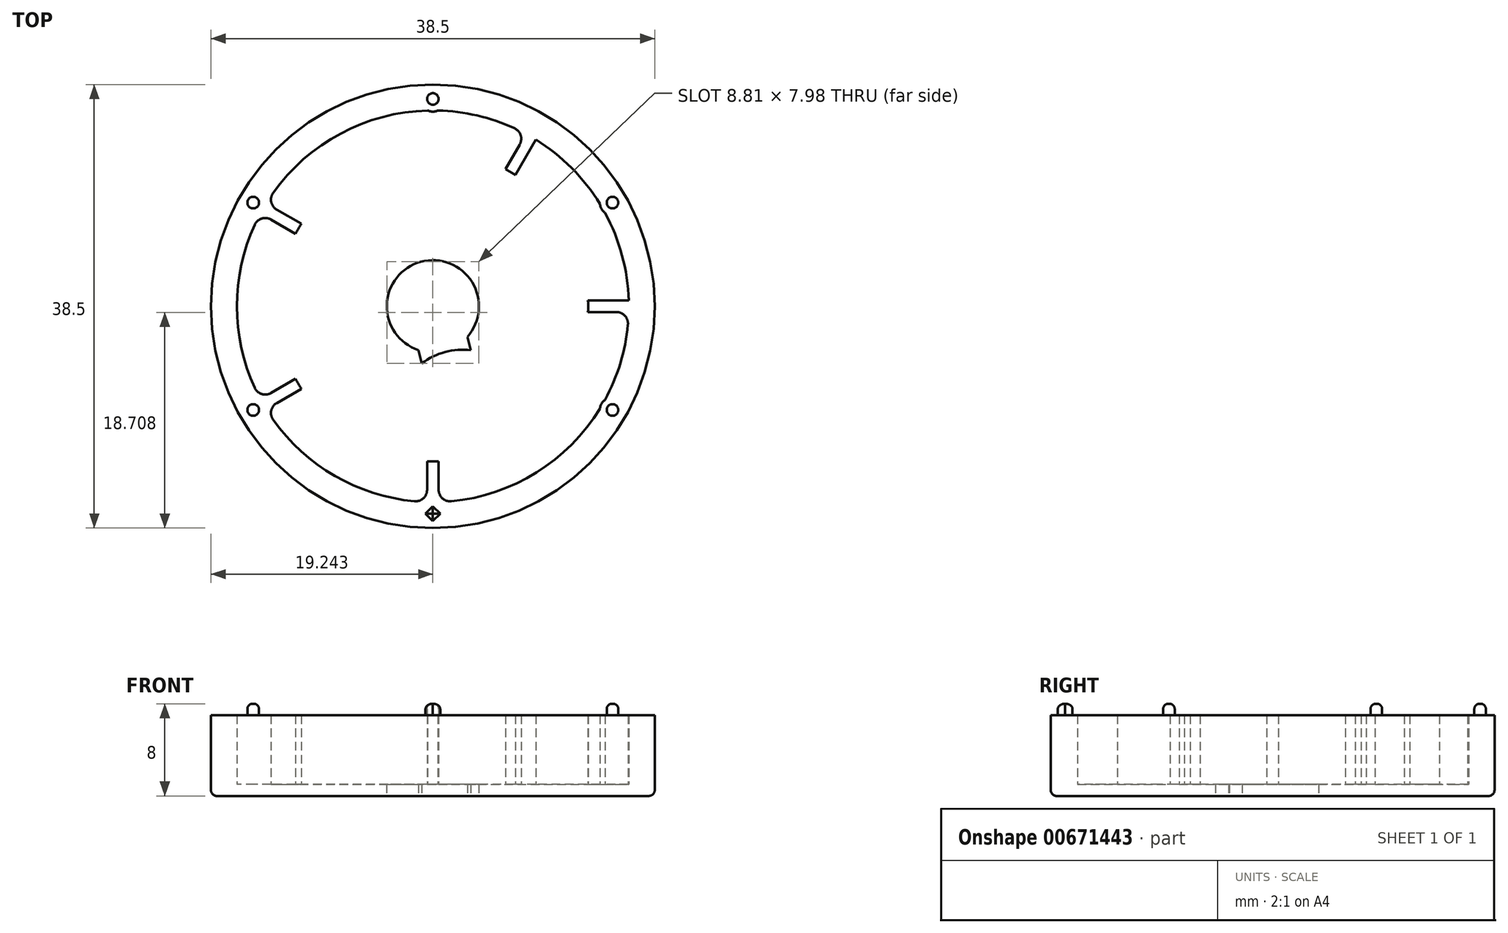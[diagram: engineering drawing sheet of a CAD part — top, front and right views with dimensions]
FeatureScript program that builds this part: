
annotation { "Feature Type Name" : "Feature", "Feature Type Description" : "" }
export const myFeature = defineFeature(function(context is Context, id is Id, definition is map)
    precondition{}
    {
        {
            var Q0;
            Q0=qCreatedBy(makeId("Top.planeOp"),FACE);
            var sketch = newSketch(context, id + "F0", { "sketchPlane" : qUnion([Q0])});
            skCircle(sketch, "E0", {"center": v(0, 0) * mm, "radius": 18 * mm});
            skCircle(sketch, "E1.0", {"center": v(0, 0) * mm, "radius": 17 * mm});
            skLineSegment(sketch, "E2.bottom", {"start": v(8.56, 15.83) * mm, "end": v(9.43, 15.33) * mm});
            skLineSegment(sketch, "E2.top", {"start": v(-9.43, -15.33) * mm, "end": v(-8.56, -15.83) * mm});
            skLineSegment(sketch, "E2.left", {"start": v(8.56, 15.83) * mm, "end": v(-9.43, -15.33) * mm});
            skLineSegment(sketch, "E2.right", {"start": v(9.43, 15.33) * mm, "end": v(-8.56, -15.83) * mm});
            skLineSegment(sketch, "E3.bottom", {"start": v(15.33, 9.43) * mm, "end": v(15.83, 8.56) * mm});
            skLineSegment(sketch, "E3.top", {"start": v(-15.83, -8.56) * mm, "end": v(-15.33, -9.43) * mm});
            skLineSegment(sketch, "E3.left", {"start": v(15.33, 9.43) * mm, "end": v(-15.83, -8.56) * mm});
            skLineSegment(sketch, "E3.right", {"start": v(15.83, 8.56) * mm, "end": v(-15.33, -9.43) * mm});
            skLineSegment(sketch, "E4", {"start": v(-38.35, 0) * mm, "end": v(39.17, 0) * mm, "construction": true});
            skLineSegment(sketch, "E5", {"start": v(0, 42.5) * mm, "end": v(0, -42.47) * mm, "construction": true});
            skLineSegment(sketch, "E6.bottom", {"start": v(-18, 0.5) * mm, "end": v(18, 0.5) * mm});
            skLineSegment(sketch, "E6.top", {"start": v(-18, -0.5) * mm, "end": v(18, -0.5) * mm});
            skLineSegment(sketch, "E6.left", {"start": v(-18, 0.5) * mm, "end": v(-18, -0.5) * mm});
            skLineSegment(sketch, "E6.right", {"start": v(18, 0.5) * mm, "end": v(18, -0.5) * mm});
            skLineSegment(sketch, "E7.bottom", {"start": v(-15.33, 9.43) * mm, "end": v(15.83, -8.56) * mm});
            skLineSegment(sketch, "E7.top", {"start": v(-15.83, 8.56) * mm, "end": v(15.33, -9.43) * mm});
            skLineSegment(sketch, "E7.left", {"start": v(-15.33, 9.43) * mm, "end": v(-15.83, 8.56) * mm});
            skLineSegment(sketch, "E7.right", {"start": v(15.83, -8.56) * mm, "end": v(15.33, -9.43) * mm});
            skLineSegment(sketch, "E8.bottom", {"start": v(-0.5, 18) * mm, "end": v(0.5, 18) * mm});
            skLineSegment(sketch, "E8.top", {"start": v(-0.5, -18) * mm, "end": v(0.5, -18) * mm});
            skLineSegment(sketch, "E8.left", {"start": v(-0.5, 18) * mm, "end": v(-0.5, -18) * mm});
            skLineSegment(sketch, "E8.right", {"start": v(0.5, 18) * mm, "end": v(0.5, -18) * mm});
            skLineSegment(sketch, "E9.bottom", {"start": v(-9.43, 15.33) * mm, "end": v(-8.56, 15.83) * mm});
            skLineSegment(sketch, "E9.top", {"start": v(8.56, -15.83) * mm, "end": v(9.43, -15.33) * mm});
            skLineSegment(sketch, "E9.left", {"start": v(-9.43, 15.33) * mm, "end": v(8.56, -15.83) * mm});
            skLineSegment(sketch, "E9.right", {"start": v(-8.56, 15.83) * mm, "end": v(9.43, -15.33) * mm});
            skCircle(sketch, "E10", {"center": v(0, 0) * mm, "radius": 13.47 * mm});
            skSolve(sketch);
        }
        {
            var Q0;
            Q0=qCreatedBy(makeId("Top.planeOp"),FACE);
            var sketch = newSketch(context, id + "F1", { "sketchPlane" : qUnion([Q0])});
            skCircle(sketch, "E11", {"center": v(0, 0) * mm, "radius": 19.25 * mm});
            skCircle(sketch, "E12", {"center": v(0, 0) * mm, "radius": 17 * mm});
            skSolve(sketch);
        }
        {
            var Q0;
            Q0=makeQuery(id+"F1.imprint","IMPRINT",FACE,{"disambiguationData":[TD([[makeQuery(id+"F1.imprint","IMPRINT",EDGE,{"derivedFrom":sQuery(id+"F1.wireOp",EDGE,"E11")}),1.0]])]});
            extrude(context, id + "F2", {"entities" : qUnion([Q0]), "depth" : 7 * mm, "offsetDistance" : 25 * mm});
        }
        {
            var Q0;
            Q0=qSketchRegion(id+"F1",true);
            var Q1;
            {var subQ0=sQuery(id+"F0.wireOp",EDGE,"E7.bottom");var subQ1=sQuery(id+"F0.wireOp",EDGE,"E1.0");var subQ2=makeQuery(id+"F0.imprint","INTERSECT",VERTEX,{"disambiguationData":[OD(0.0)],"derivedFrom":[subQ1,subQ0]});Q1=makeQuery(id+"F0.imprint","IMPRINT",FACE,{"disambiguationData":[TD([[makeQuery(id+"F0.imprint","IMPRINT",EDGE,{"disambiguationData":[TD([[subQ2,-1.0]])],"derivedFrom":subQ1}),1.0]])]});}
            var Q2;
            {var subQ0=sQuery(id+"F0.wireOp",EDGE,"E2.right");var subQ1=sQuery(id+"F0.wireOp",EDGE,"E1.0");var subQ2=makeQuery(id+"F0.imprint","INTERSECT",VERTEX,{"disambiguationData":[OD(0.0)],"derivedFrom":[subQ1,subQ0]});Q2=makeQuery(id+"F0.imprint","IMPRINT",FACE,{"disambiguationData":[TD([[makeQuery(id+"F0.imprint","IMPRINT",EDGE,{"disambiguationData":[TD([[subQ2,-1.0]])],"derivedFrom":subQ1}),1.0]])]});}
            var Q3;
            {var subQ0=sQuery(id+"F0.wireOp",EDGE,"E6.bottom");var subQ1=sQuery(id+"F0.wireOp",EDGE,"E1.0");var subQ2=makeQuery(id+"F0.imprint","INTERSECT",VERTEX,{"disambiguationData":[OD(0.0)],"derivedFrom":[subQ1,subQ0]});Q3=makeQuery(id+"F0.imprint","IMPRINT",FACE,{"disambiguationData":[TD([[makeQuery(id+"F0.imprint","IMPRINT",EDGE,{"disambiguationData":[TD([[subQ2,1.0]])],"derivedFrom":subQ1}),1.0]])]});}
            var Q4;
            {var subQ0=sQuery(id+"F0.wireOp",EDGE,"E8.left");var subQ1=sQuery(id+"F0.wireOp",EDGE,"E1.0");var subQ2=makeQuery(id+"F0.imprint","INTERSECT",VERTEX,{"disambiguationData":[OD(1.0)],"derivedFrom":[subQ1,subQ0]});Q4=makeQuery(id+"F0.imprint","IMPRINT",FACE,{"disambiguationData":[TD([[makeQuery(id+"F0.imprint","IMPRINT",EDGE,{"disambiguationData":[TD([[subQ2,-1.0]])],"derivedFrom":subQ1}),1.0]])]});}
            var Q5;
            {var subQ0=sQuery(id+"F0.wireOp",EDGE,"E3.left");var subQ1=sQuery(id+"F0.wireOp",EDGE,"E1.0");var subQ2=makeQuery(id+"F0.imprint","INTERSECT",VERTEX,{"disambiguationData":[OD(1.0)],"derivedFrom":[subQ1,subQ0]});Q5=makeQuery(id+"F0.imprint","IMPRINT",FACE,{"disambiguationData":[TD([[makeQuery(id+"F0.imprint","IMPRINT",EDGE,{"disambiguationData":[TD([[subQ2,-1.0]])],"derivedFrom":subQ1}),1.0]])]});}
            extrude(context, id + "F3", {"entities" : qUnion([Q0, Q1, Q2, Q3, Q4, Q5]), "operationType" : NewBodyOperationType.ADD, "depth" : 7 * mm, "offsetDistance" : 25 * mm});
        }
        {
            var Q0;
            Q0=makeQuery(id+"F1.imprint","IMPRINT",FACE,{"disambiguationData":[TD([[makeQuery(id+"F1.imprint","IMPRINT",EDGE,{"derivedFrom":sQuery(id+"F1.wireOp",EDGE,"E11")}),1.0]])]});
            var Q1;
            Q1=makeQuery(id+"F1.imprint","IMPRINT",FACE,{"disambiguationData":[TD([[makeQuery(id+"F1.imprint","IMPRINT",EDGE,{"derivedFrom":sQuery(id+"F1.wireOp",EDGE,"E12")}),1.0]])]});
            extrude(context, id + "F4", {"entities" : qUnion([Q0, Q1]), "operationType" : NewBodyOperationType.ADD, "depth" : 1 * mm, "offsetDistance" : 25 * mm});
        }
        {
            var Q0;
            Q0=qCreatedBy(makeId("Top.planeOp"),FACE);
            var sketch = newSketch(context, id + "F5", { "sketchPlane" : qUnion([Q0])});
            skCircle(sketch, "E13", {"center": v(0, 0) * mm, "radius": 18 * mm});
            skLineSegment(sketch, "E14", {"start": v(0, 18) * mm, "end": v(0, -18) * mm, "construction": true});
            skLineSegment(sketch, "E15", {"start": v(15.59, 9) * mm, "end": v(0, 0) * mm, "construction": true});
            skLineSegment(sketch, "E16", {"start": v(9, 15.59) * mm, "end": v(0, 0) * mm, "construction": true});
            skLineSegment(sketch, "E17", {"start": v(0, 0) * mm, "end": v(18, 0) * mm, "construction": true});
            skLineSegment(sketch, "E18", {"start": v(0, 0) * mm, "end": v(15.59, -9) * mm, "construction": true});
            skLineSegment(sketch, "E19", {"start": v(0, 0) * mm, "end": v(9, -15.59) * mm, "construction": true});
            skLineSegment(sketch, "E20", {"start": v(0, 0) * mm, "end": v(-9, 15.59) * mm, "construction": true});
            skLineSegment(sketch, "E21", {"start": v(0, 0) * mm, "end": v(-15.59, 9) * mm, "construction": true});
            skLineSegment(sketch, "E22", {"start": v(0, 0) * mm, "end": v(-18, 0) * mm, "construction": true});
            skLineSegment(sketch, "E23", {"start": v(0, 0) * mm, "end": v(-15.59, -9) * mm, "construction": true});
            skLineSegment(sketch, "E24", {"start": v(0, 0) * mm, "end": v(-9, -15.59) * mm, "construction": true});
            skCircle(sketch, "E25", {"center": v(0, 18) * mm, "radius": 1.1 * mm});
            skCircle(sketch, "E26", {"center": v(15.59, 9) * mm, "radius": 1.1 * mm});
            skCircle(sketch, "E27", {"center": v(15.59, -9) * mm, "radius": 1.1 * mm});
            skCircle(sketch, "E28", {"center": v(0, -18) * mm, "radius": 1.1 * mm});
            skCircle(sketch, "E29", {"center": v(-15.59, -9) * mm, "radius": 1.1 * mm});
            skCircle(sketch, "E30", {"center": v(-15.59, 9) * mm, "radius": 1.1 * mm});
            skCircle(sketch, "E31", {"center": v(-15.59, 9) * mm, "radius": 0.5 * mm});
            skCircle(sketch, "E32", {"center": v(0, 18) * mm, "radius": 0.5 * mm});
            skCircle(sketch, "E33", {"center": v(15.59, 9) * mm, "radius": 0.5 * mm});
            skCircle(sketch, "E34", {"center": v(15.59, -9) * mm, "radius": 0.5 * mm});
            skCircle(sketch, "E35", {"center": v(-15.59, -9) * mm, "radius": 0.5 * mm});
            skLineSegment(sketch, "E36.bottom", {"start": v(0.64, -18) * mm, "end": v(0, -18.64) * mm});
            skLineSegment(sketch, "E36.top", {"start": v(0, -17.36) * mm, "end": v(-0.64, -18) * mm});
            skLineSegment(sketch, "E36.left", {"start": v(0.64, -18) * mm, "end": v(0, -17.36) * mm});
            skLineSegment(sketch, "E36.right", {"start": v(0, -18.64) * mm, "end": v(-0.64, -18) * mm});
            skSolve(sketch);
        }
        {
            var Q0;
            {var subQ0=sQuery(id+"F5.wireOp",EDGE,"E30");var subQ1=sQuery(id+"F5.wireOp",EDGE,"E13");var subQ2=makeQuery(id+"F5.imprint","INTERSECT",VERTEX,{"disambiguationData":[OD(0.0)],"derivedFrom":[subQ1,subQ0]});Q0=makeQuery(id+"F5.imprint","IMPRINT",FACE,{"disambiguationData":[TD([[makeQuery(id+"F5.imprint","IMPRINT",EDGE,{"disambiguationData":[TD([[subQ2,-1.0]])],"derivedFrom":subQ1}),1.0]])]});}
            var Q1;
            {var subQ0=sQuery(id+"F5.wireOp",EDGE,"E30");var subQ1=sQuery(id+"F5.wireOp",EDGE,"E13");var subQ2=makeQuery(id+"F5.imprint","INTERSECT",VERTEX,{"disambiguationData":[OD(0.0)],"derivedFrom":[subQ1,subQ0]});Q1=makeQuery(id+"F5.imprint","IMPRINT",FACE,{"disambiguationData":[TD([[makeQuery(id+"F5.imprint","IMPRINT",EDGE,{"disambiguationData":[TD([[subQ2,-1.0]])],"derivedFrom":subQ1}),-1.0]])]});}
            var Q2;
            {var subQ0=sQuery(id+"F5.wireOp",EDGE,"E25");var subQ1=sQuery(id+"F5.wireOp",EDGE,"E13");var subQ2=makeQuery(id+"F5.imprint","INTERSECT",VERTEX,{"disambiguationData":[OD(0.0)],"derivedFrom":[subQ1,subQ0]});Q2=makeQuery(id+"F5.imprint","IMPRINT",FACE,{"disambiguationData":[TD([[makeQuery(id+"F5.imprint","IMPRINT",EDGE,{"disambiguationData":[TD([[subQ2,-1.0]])],"derivedFrom":subQ1}),1.0]])]});}
            var Q3;
            {var subQ0=sQuery(id+"F5.wireOp",EDGE,"E25");var subQ1=sQuery(id+"F5.wireOp",EDGE,"E13");var subQ2=makeQuery(id+"F5.imprint","INTERSECT",VERTEX,{"disambiguationData":[OD(0.0)],"derivedFrom":[subQ1,subQ0]});Q3=makeQuery(id+"F5.imprint","IMPRINT",FACE,{"disambiguationData":[TD([[makeQuery(id+"F5.imprint","IMPRINT",EDGE,{"disambiguationData":[TD([[subQ2,-1.0]])],"derivedFrom":subQ1}),-1.0]])]});}
            var Q4;
            {var subQ0=sQuery(id+"F5.wireOp",EDGE,"E26");var subQ1=sQuery(id+"F5.wireOp",EDGE,"E13");var subQ2=makeQuery(id+"F5.imprint","INTERSECT",VERTEX,{"disambiguationData":[OD(0.0)],"derivedFrom":[subQ1,subQ0]});Q4=makeQuery(id+"F5.imprint","IMPRINT",FACE,{"disambiguationData":[TD([[makeQuery(id+"F5.imprint","IMPRINT",EDGE,{"disambiguationData":[TD([[subQ2,-1.0]])],"derivedFrom":subQ1}),-1.0]])]});}
            var Q5;
            {var subQ0=sQuery(id+"F5.wireOp",EDGE,"E26");var subQ1=sQuery(id+"F5.wireOp",EDGE,"E13");var subQ2=makeQuery(id+"F5.imprint","INTERSECT",VERTEX,{"disambiguationData":[OD(0.0)],"derivedFrom":[subQ1,subQ0]});Q5=makeQuery(id+"F5.imprint","IMPRINT",FACE,{"disambiguationData":[TD([[makeQuery(id+"F5.imprint","IMPRINT",EDGE,{"disambiguationData":[TD([[subQ2,-1.0]])],"derivedFrom":subQ1}),1.0]])]});}
            var Q6;
            {var subQ0=sQuery(id+"F5.wireOp",EDGE,"E29");var subQ1=sQuery(id+"F5.wireOp",EDGE,"E13");var subQ2=makeQuery(id+"F5.imprint","INTERSECT",VERTEX,{"disambiguationData":[OD(0.0)],"derivedFrom":[subQ1,subQ0]});Q6=makeQuery(id+"F5.imprint","IMPRINT",FACE,{"disambiguationData":[TD([[makeQuery(id+"F5.imprint","IMPRINT",EDGE,{"disambiguationData":[TD([[subQ2,-1.0]])],"derivedFrom":subQ1}),1.0]])]});}
            var Q7;
            {var subQ0=sQuery(id+"F5.wireOp",EDGE,"E29");var subQ1=sQuery(id+"F5.wireOp",EDGE,"E13");var subQ2=makeQuery(id+"F5.imprint","INTERSECT",VERTEX,{"disambiguationData":[OD(0.0)],"derivedFrom":[subQ1,subQ0]});Q7=makeQuery(id+"F5.imprint","IMPRINT",FACE,{"disambiguationData":[TD([[makeQuery(id+"F5.imprint","IMPRINT",EDGE,{"disambiguationData":[TD([[subQ2,-1.0]])],"derivedFrom":subQ1}),-1.0]])]});}
            var Q8;
            {var subQ3=sQuery(id+"F5.wireOp",EDGE,"E13");var subQ5=sQuery(id+"F5.wireOp",EDGE,"E28");var subQ6=makeQuery(id+"F5.imprint","INTERSECT",VERTEX,{"disambiguationData":[OD(0.0)],"derivedFrom":[subQ3,subQ5]});Q8=makeQuery(id+"F5.imprint","IMPRINT",FACE,{"disambiguationData":[TD([[makeQuery(id+"F5.imprint","IMPRINT",EDGE,{"disambiguationData":[TD([[subQ6,-1.0]])],"derivedFrom":subQ3}),1.0]])]});}
            var Q9;
            {var subQ6=sQuery(id+"F5.wireOp",EDGE,"E36.bottom");Q9=makeQuery(id+"F5.imprint","IMPRINT",FACE,{"disambiguationData":[TD([[makeQuery(id+"F5.imprint","IMPRINT",EDGE,{"derivedFrom":subQ6}),1.0]])]});}
            var Q10;
            {var subQ0=sQuery(id+"F5.wireOp",EDGE,"E27");var subQ1=sQuery(id+"F5.wireOp",EDGE,"E13");var subQ2=makeQuery(id+"F5.imprint","INTERSECT",VERTEX,{"disambiguationData":[OD(0.0)],"derivedFrom":[subQ1,subQ0]});Q10=makeQuery(id+"F5.imprint","IMPRINT",FACE,{"disambiguationData":[TD([[makeQuery(id+"F5.imprint","IMPRINT",EDGE,{"disambiguationData":[TD([[subQ2,-1.0]])],"derivedFrom":subQ1}),-1.0]])]});}
            var Q11;
            {var subQ0=sQuery(id+"F5.wireOp",EDGE,"E27");var subQ1=sQuery(id+"F5.wireOp",EDGE,"E13");var subQ2=makeQuery(id+"F5.imprint","INTERSECT",VERTEX,{"disambiguationData":[OD(0.0)],"derivedFrom":[subQ1,subQ0]});Q11=makeQuery(id+"F5.imprint","IMPRINT",FACE,{"disambiguationData":[TD([[makeQuery(id+"F5.imprint","IMPRINT",EDGE,{"disambiguationData":[TD([[subQ2,-1.0]])],"derivedFrom":subQ1}),1.0]])]});}
            var Q12;
            {var subQ0=sQuery(id+"F5.wireOp",EDGE,"E31");var subQ1=sQuery(id+"F5.wireOp",EDGE,"E13");var subQ2=makeQuery(id+"F5.imprint","INTERSECT",VERTEX,{"disambiguationData":[OD(0.0)],"derivedFrom":[subQ1,subQ0]});Q12=makeQuery(id+"F5.imprint","IMPRINT",FACE,{"disambiguationData":[TD([[makeQuery(id+"F5.imprint","IMPRINT",EDGE,{"disambiguationData":[TD([[subQ2,-1.0]])],"derivedFrom":subQ1}),1.0]])]});}
            var Q13;
            {var subQ0=sQuery(id+"F5.wireOp",EDGE,"E31");var subQ1=sQuery(id+"F5.wireOp",EDGE,"E13");var subQ2=makeQuery(id+"F5.imprint","INTERSECT",VERTEX,{"disambiguationData":[OD(0.0)],"derivedFrom":[subQ1,subQ0]});Q13=makeQuery(id+"F5.imprint","IMPRINT",FACE,{"disambiguationData":[TD([[makeQuery(id+"F5.imprint","IMPRINT",EDGE,{"disambiguationData":[TD([[subQ2,-1.0]])],"derivedFrom":subQ1}),-1.0]])]});}
            var Q14;
            {var subQ0=sQuery(id+"F5.wireOp",EDGE,"E32");var subQ1=sQuery(id+"F5.wireOp",EDGE,"E13");var subQ2=makeQuery(id+"F5.imprint","INTERSECT",VERTEX,{"disambiguationData":[OD(0.0)],"derivedFrom":[subQ1,subQ0]});Q14=makeQuery(id+"F5.imprint","IMPRINT",FACE,{"disambiguationData":[TD([[makeQuery(id+"F5.imprint","IMPRINT",EDGE,{"disambiguationData":[TD([[subQ2,-1.0]])],"derivedFrom":subQ1}),-1.0]])]});}
            var Q15;
            {var subQ0=sQuery(id+"F5.wireOp",EDGE,"E32");var subQ1=sQuery(id+"F5.wireOp",EDGE,"E13");var subQ2=makeQuery(id+"F5.imprint","INTERSECT",VERTEX,{"disambiguationData":[OD(0.0)],"derivedFrom":[subQ1,subQ0]});Q15=makeQuery(id+"F5.imprint","IMPRINT",FACE,{"disambiguationData":[TD([[makeQuery(id+"F5.imprint","IMPRINT",EDGE,{"disambiguationData":[TD([[subQ2,-1.0]])],"derivedFrom":subQ1}),1.0]])]});}
            var Q16;
            {var subQ0=sQuery(id+"F5.wireOp",EDGE,"E33");var subQ1=sQuery(id+"F5.wireOp",EDGE,"E13");var subQ2=makeQuery(id+"F5.imprint","INTERSECT",VERTEX,{"disambiguationData":[OD(0.0)],"derivedFrom":[subQ1,subQ0]});Q16=makeQuery(id+"F5.imprint","IMPRINT",FACE,{"disambiguationData":[TD([[makeQuery(id+"F5.imprint","IMPRINT",EDGE,{"disambiguationData":[TD([[subQ2,-1.0]])],"derivedFrom":subQ1}),-1.0]])]});}
            var Q17;
            {var subQ0=sQuery(id+"F5.wireOp",EDGE,"E33");var subQ1=sQuery(id+"F5.wireOp",EDGE,"E13");var subQ2=makeQuery(id+"F5.imprint","INTERSECT",VERTEX,{"disambiguationData":[OD(0.0)],"derivedFrom":[subQ1,subQ0]});Q17=makeQuery(id+"F5.imprint","IMPRINT",FACE,{"disambiguationData":[TD([[makeQuery(id+"F5.imprint","IMPRINT",EDGE,{"disambiguationData":[TD([[subQ2,-1.0]])],"derivedFrom":subQ1}),1.0]])]});}
            var Q18;
            {var subQ0=sQuery(id+"F5.wireOp",EDGE,"E34");var subQ1=sQuery(id+"F5.wireOp",EDGE,"E13");var subQ2=makeQuery(id+"F5.imprint","INTERSECT",VERTEX,{"disambiguationData":[OD(0.0)],"derivedFrom":[subQ1,subQ0]});Q18=makeQuery(id+"F5.imprint","IMPRINT",FACE,{"disambiguationData":[TD([[makeQuery(id+"F5.imprint","IMPRINT",EDGE,{"disambiguationData":[TD([[subQ2,-1.0]])],"derivedFrom":subQ1}),-1.0]])]});}
            var Q19;
            {var subQ0=sQuery(id+"F5.wireOp",EDGE,"E34");var subQ1=sQuery(id+"F5.wireOp",EDGE,"E13");var subQ2=makeQuery(id+"F5.imprint","INTERSECT",VERTEX,{"disambiguationData":[OD(0.0)],"derivedFrom":[subQ1,subQ0]});Q19=makeQuery(id+"F5.imprint","IMPRINT",FACE,{"disambiguationData":[TD([[makeQuery(id+"F5.imprint","IMPRINT",EDGE,{"disambiguationData":[TD([[subQ2,-1.0]])],"derivedFrom":subQ1}),1.0]])]});}
            var Q20;
            {var subQ1=sQuery(id+"F5.wireOp",EDGE,"E36.bottom");Q20=makeQuery(id+"F5.imprint","IMPRINT",FACE,{"disambiguationData":[TD([[makeQuery(id+"F5.imprint","IMPRINT",EDGE,{"derivedFrom":subQ1}),-1.0]])]});}
            var Q21;
            {var subQ0=sQuery(id+"F5.wireOp",EDGE,"E35");var subQ1=sQuery(id+"F5.wireOp",EDGE,"E13");var subQ2=makeQuery(id+"F5.imprint","INTERSECT",VERTEX,{"disambiguationData":[OD(0.0)],"derivedFrom":[subQ1,subQ0]});Q21=makeQuery(id+"F5.imprint","IMPRINT",FACE,{"disambiguationData":[TD([[makeQuery(id+"F5.imprint","IMPRINT",EDGE,{"disambiguationData":[TD([[subQ2,-1.0]])],"derivedFrom":subQ1}),-1.0]])]});}
            var Q22;
            {var subQ0=sQuery(id+"F5.wireOp",EDGE,"E35");var subQ1=sQuery(id+"F5.wireOp",EDGE,"E13");var subQ2=makeQuery(id+"F5.imprint","INTERSECT",VERTEX,{"disambiguationData":[OD(0.0)],"derivedFrom":[subQ1,subQ0]});Q22=makeQuery(id+"F5.imprint","IMPRINT",FACE,{"disambiguationData":[TD([[makeQuery(id+"F5.imprint","IMPRINT",EDGE,{"disambiguationData":[TD([[subQ2,-1.0]])],"derivedFrom":subQ1}),1.0]])]});}
            var Q23;
            {var subQ0=sQuery(id+"F5.wireOp",EDGE,"E36.top");var subQ1=sQuery(id+"F5.wireOp",EDGE,"E13");var subQ2=makeQuery(id+"F5.imprint","INTERSECT",VERTEX,{"derivedFrom":[subQ1,subQ0]});Q23=makeQuery(id+"F5.imprint","IMPRINT",FACE,{"disambiguationData":[TD([[makeQuery(id+"F5.imprint","IMPRINT",EDGE,{"disambiguationData":[TD([[subQ2,-1.0]])],"derivedFrom":subQ1}),1.0]])]});}
            extrude(context, id + "F6", {"entities" : qUnion([Q0, Q1, Q2, Q3, Q4, Q5, Q6, Q7, Q8, Q9, Q10, Q11, Q12, Q13, Q14, Q15, Q16, Q17, Q18, Q19, Q20, Q21, Q22, Q23]), "operationType" : NewBodyOperationType.ADD, "depth" : 7 * mm, "offsetDistance" : 25 * mm});
        }
        {
            var Q0;
            {var subQ0=sQuery(id+"F0.wireOp",EDGE,"E8.right");var subQ1=sQuery(id+"F0.wireOp",EDGE,"E1.0");Q0=makeQuery(id+"F3.opExtrude","SWEPT_EDGE",EDGE,{"disambiguationData":[OSD([subQ1,subQ0]),TDD([makeQuery(id+"F0.imprint","INTERSECT",VERTEX,{"disambiguationData":[OD(1.0)],"derivedFrom":[subQ1,subQ0]})])]});}
            var Q1;
            {var subQ0=sQuery(id+"F0.wireOp",EDGE,"E2.left");var subQ1=sQuery(id+"F0.wireOp",EDGE,"E1.0");Q1=makeQuery(id+"F3.opExtrude","SWEPT_EDGE",EDGE,{"disambiguationData":[OSD([subQ1,subQ0]),TDD([makeQuery(id+"F0.imprint","INTERSECT",VERTEX,{"disambiguationData":[OD(1.0)],"derivedFrom":[subQ1,subQ0]})])]});}
            var Q2;
            {var subQ0=sQuery(id+"F0.wireOp",EDGE,"E3.left");var subQ1=sQuery(id+"F0.wireOp",EDGE,"E1.0");Q2=makeQuery(id+"F3.opExtrude","SWEPT_EDGE",EDGE,{"disambiguationData":[OSD([subQ1,subQ0]),TDD([makeQuery(id+"F0.imprint","INTERSECT",VERTEX,{"disambiguationData":[OD(1.0)],"derivedFrom":[subQ1,subQ0]})])]});}
            var Q3;
            {var subQ0=sQuery(id+"F0.wireOp",EDGE,"E6.bottom");var subQ1=sQuery(id+"F0.wireOp",EDGE,"E1.0");Q3=makeQuery(id+"F3.opExtrude","SWEPT_EDGE",EDGE,{"disambiguationData":[OSD([subQ1,subQ0]),TDD([makeQuery(id+"F0.imprint","INTERSECT",VERTEX,{"disambiguationData":[OD(1.0)],"derivedFrom":[subQ1,subQ0]})])]});}
            var Q4;
            {var subQ0=sQuery(id+"F0.wireOp",EDGE,"E9.right");var subQ1=sQuery(id+"F0.wireOp",EDGE,"E1.0");Q4=makeQuery(id+"F3.opExtrude","SWEPT_EDGE",EDGE,{"disambiguationData":[OSD([subQ1,subQ0]),TDD([makeQuery(id+"F0.imprint","INTERSECT",VERTEX,{"disambiguationData":[OD(1.0)],"derivedFrom":[subQ1,subQ0]})])]});}
            var Q5;
            {var subQ0=sQuery(id+"F0.wireOp",EDGE,"E7.bottom");var subQ1=sQuery(id+"F0.wireOp",EDGE,"E1.0");Q5=makeQuery(id+"F3.opExtrude","SWEPT_EDGE",EDGE,{"disambiguationData":[OSD([subQ1,subQ0]),TDD([makeQuery(id+"F0.imprint","INTERSECT",VERTEX,{"disambiguationData":[OD(1.0)],"derivedFrom":[subQ1,subQ0]})])]});}
            var Q6;
            {var subQ0=sQuery(id+"F0.wireOp",EDGE,"E8.left");var subQ1=sQuery(id+"F0.wireOp",EDGE,"E1.0");Q6=makeQuery(id+"F3.opExtrude","SWEPT_EDGE",EDGE,{"disambiguationData":[OSD([subQ1,subQ0]),TDD([makeQuery(id+"F0.imprint","INTERSECT",VERTEX,{"disambiguationData":[OD(0.0)],"derivedFrom":[subQ1,subQ0]})])]});}
            var Q7;
            {var subQ0=sQuery(id+"F0.wireOp",EDGE,"E2.left");var subQ1=sQuery(id+"F0.wireOp",EDGE,"E1.0");Q7=makeQuery(id+"F3.opExtrude","SWEPT_EDGE",EDGE,{"disambiguationData":[OSD([subQ1,subQ0]),TDD([makeQuery(id+"F0.imprint","INTERSECT",VERTEX,{"disambiguationData":[OD(0.0)],"derivedFrom":[subQ1,subQ0]})])]});}
            var Q8;
            {var subQ0=sQuery(id+"F0.wireOp",EDGE,"E3.left");var subQ1=sQuery(id+"F0.wireOp",EDGE,"E1.0");Q8=makeQuery(id+"F3.opExtrude","SWEPT_EDGE",EDGE,{"disambiguationData":[OSD([subQ1,subQ0]),TDD([makeQuery(id+"F0.imprint","INTERSECT",VERTEX,{"disambiguationData":[OD(0.0)],"derivedFrom":[subQ1,subQ0]})])]});}
            var Q9;
            {var subQ0=sQuery(id+"F0.wireOp",EDGE,"E6.top");var subQ1=sQuery(id+"F0.wireOp",EDGE,"E1.0");Q9=makeQuery(id+"F3.opExtrude","SWEPT_EDGE",EDGE,{"disambiguationData":[OSD([subQ1,subQ0]),TDD([makeQuery(id+"F0.imprint","INTERSECT",VERTEX,{"disambiguationData":[OD(1.0)],"derivedFrom":[subQ1,subQ0]})])]});}
            var Q10;
            {var subQ0=sQuery(id+"F0.wireOp",EDGE,"E7.top");var subQ1=sQuery(id+"F0.wireOp",EDGE,"E1.0");Q10=makeQuery(id+"F3.opExtrude","SWEPT_EDGE",EDGE,{"disambiguationData":[OSD([subQ1,subQ0]),TDD([makeQuery(id+"F0.imprint","INTERSECT",VERTEX,{"disambiguationData":[OD(0.0)],"derivedFrom":[subQ1,subQ0]})])]});}
            var Q11;
            {var subQ0=sQuery(id+"F0.wireOp",EDGE,"E6.top");var subQ1=sQuery(id+"F0.wireOp",EDGE,"E1.0");Q11=makeQuery(id+"F3.opExtrude","SWEPT_EDGE",EDGE,{"disambiguationData":[OSD([subQ1,subQ0]),TDD([makeQuery(id+"F0.imprint","INTERSECT",VERTEX,{"disambiguationData":[OD(0.0)],"derivedFrom":[subQ1,subQ0]})])]});}
            var Q12;
            {var subQ0=sQuery(id+"F0.wireOp",EDGE,"E9.left");var subQ1=sQuery(id+"F0.wireOp",EDGE,"E1.0");Q12=makeQuery(id+"F3.opExtrude","SWEPT_EDGE",EDGE,{"disambiguationData":[OSD([subQ1,subQ0]),TDD([makeQuery(id+"F0.imprint","INTERSECT",VERTEX,{"disambiguationData":[OD(0.0)],"derivedFrom":[subQ1,subQ0]})])]});}
            var Q13;
            {var subQ0=sQuery(id+"F0.wireOp",EDGE,"E8.right");var subQ1=sQuery(id+"F0.wireOp",EDGE,"E1.0");Q13=makeQuery(id+"F3.opExtrude","SWEPT_EDGE",EDGE,{"disambiguationData":[OSD([subQ1,subQ0]),TDD([makeQuery(id+"F0.imprint","INTERSECT",VERTEX,{"disambiguationData":[OD(0.0)],"derivedFrom":[subQ1,subQ0]})])]});}
            var Q14;
            {var subQ0=sQuery(id+"F0.wireOp",EDGE,"E7.bottom");var subQ1=sQuery(id+"F0.wireOp",EDGE,"E1.0");Q14=makeQuery(id+"F3.opExtrude","SWEPT_EDGE",EDGE,{"disambiguationData":[OSD([subQ1,subQ0]),TDD([makeQuery(id+"F0.imprint","INTERSECT",VERTEX,{"disambiguationData":[OD(0.0)],"derivedFrom":[subQ1,subQ0]})])]});}
            var Q15;
            {var subQ0=sQuery(id+"F0.wireOp",EDGE,"E9.right");var subQ1=sQuery(id+"F0.wireOp",EDGE,"E1.0");Q15=makeQuery(id+"F3.opExtrude","SWEPT_EDGE",EDGE,{"disambiguationData":[OSD([subQ1,subQ0]),TDD([makeQuery(id+"F0.imprint","INTERSECT",VERTEX,{"disambiguationData":[OD(0.0)],"derivedFrom":[subQ1,subQ0]})])]});}
            var Q16;
            {var subQ0=sQuery(id+"F0.wireOp",EDGE,"E3.right");var subQ1=sQuery(id+"F0.wireOp",EDGE,"E1.0");Q16=makeQuery(id+"F3.opExtrude","SWEPT_EDGE",EDGE,{"disambiguationData":[OSD([subQ1,subQ0]),TDD([makeQuery(id+"F0.imprint","INTERSECT",VERTEX,{"disambiguationData":[OD(1.0)],"derivedFrom":[subQ1,subQ0]})])]});}
            var Q17;
            {var subQ0=sQuery(id+"F0.wireOp",EDGE,"E2.right");var subQ1=sQuery(id+"F0.wireOp",EDGE,"E1.0");Q17=makeQuery(id+"F3.opExtrude","SWEPT_EDGE",EDGE,{"disambiguationData":[OSD([subQ1,subQ0]),TDD([makeQuery(id+"F0.imprint","INTERSECT",VERTEX,{"disambiguationData":[OD(1.0)],"derivedFrom":[subQ1,subQ0]})])]});}
            var Q18;
            {var subQ0=sQuery(id+"F0.wireOp",EDGE,"E3.right");var subQ1=sQuery(id+"F0.wireOp",EDGE,"E1.0");Q18=makeQuery(id+"F3.opExtrude","SWEPT_EDGE",EDGE,{"disambiguationData":[OSD([subQ1,subQ0]),TDD([makeQuery(id+"F0.imprint","INTERSECT",VERTEX,{"disambiguationData":[OD(0.0)],"derivedFrom":[subQ1,subQ0]})])]});}
            var Q19;
            {var subQ0=sQuery(id+"F0.wireOp",EDGE,"E2.right");var subQ1=sQuery(id+"F0.wireOp",EDGE,"E1.0");Q19=makeQuery(id+"F3.opExtrude","SWEPT_EDGE",EDGE,{"disambiguationData":[OSD([subQ1,subQ0]),TDD([makeQuery(id+"F0.imprint","INTERSECT",VERTEX,{"disambiguationData":[OD(0.0)],"derivedFrom":[subQ1,subQ0]})])]});}
            var Q20;
            {var subQ0=sQuery(id+"F0.wireOp",EDGE,"E8.left");var subQ1=sQuery(id+"F0.wireOp",EDGE,"E1.0");Q20=makeQuery(id+"F3.opExtrude","SWEPT_EDGE",EDGE,{"disambiguationData":[OSD([subQ1,subQ0]),TDD([makeQuery(id+"F0.imprint","INTERSECT",VERTEX,{"disambiguationData":[OD(1.0)],"derivedFrom":[subQ1,subQ0]})])]});}
            var Q21;
            {var subQ0=sQuery(id+"F0.wireOp",EDGE,"E9.left");var subQ1=sQuery(id+"F0.wireOp",EDGE,"E1.0");Q21=makeQuery(id+"F3.opExtrude","SWEPT_EDGE",EDGE,{"disambiguationData":[OSD([subQ1,subQ0]),TDD([makeQuery(id+"F0.imprint","INTERSECT",VERTEX,{"disambiguationData":[OD(1.0)],"derivedFrom":[subQ1,subQ0]})])]});}
            var Q22;
            {var subQ0=sQuery(id+"F0.wireOp",EDGE,"E7.top");var subQ1=sQuery(id+"F0.wireOp",EDGE,"E1.0");Q22=makeQuery(id+"F3.opExtrude","SWEPT_EDGE",EDGE,{"disambiguationData":[OSD([subQ1,subQ0]),TDD([makeQuery(id+"F0.imprint","INTERSECT",VERTEX,{"disambiguationData":[OD(1.0)],"derivedFrom":[subQ1,subQ0]})])]});}
            var Q23;
            {var subQ0=sQuery(id+"F0.wireOp",EDGE,"E6.bottom");var subQ1=sQuery(id+"F0.wireOp",EDGE,"E1.0");Q23=makeQuery(id+"F3.opExtrude","SWEPT_EDGE",EDGE,{"disambiguationData":[OSD([subQ1,subQ0]),TDD([makeQuery(id+"F0.imprint","INTERSECT",VERTEX,{"disambiguationData":[OD(0.0)],"derivedFrom":[subQ1,subQ0]})])]});}
            fillet(context, id + "F7", {"entities" : qUnion([Q0, Q1, Q2, Q3, Q4, Q5, Q6, Q7, Q8, Q9, Q10, Q11, Q12, Q13, Q14, Q15, Q16, Q17, Q18, Q19, Q20, Q21, Q22, Q23]), "radius" : 1 * mm, "tangentPropagation" : true, "allowEdgeOverflow" : false});
        }
        {
            var Q0;
            {var subQ0=sQuery(id+"F5.wireOp",EDGE,"E31");var subQ1=sQuery(id+"F5.wireOp",EDGE,"E13");var subQ2=makeQuery(id+"F5.imprint","INTERSECT",VERTEX,{"disambiguationData":[OD(0.0)],"derivedFrom":[subQ1,subQ0]});Q0=makeQuery(id+"F5.imprint","IMPRINT",FACE,{"disambiguationData":[TD([[makeQuery(id+"F5.imprint","IMPRINT",EDGE,{"disambiguationData":[TD([[subQ2,-1.0]])],"derivedFrom":subQ1}),-1.0]])]});}
            var Q1;
            {var subQ0=sQuery(id+"F5.wireOp",EDGE,"E31");var subQ1=sQuery(id+"F5.wireOp",EDGE,"E13");var subQ2=makeQuery(id+"F5.imprint","INTERSECT",VERTEX,{"disambiguationData":[OD(0.0)],"derivedFrom":[subQ1,subQ0]});Q1=makeQuery(id+"F5.imprint","IMPRINT",FACE,{"disambiguationData":[TD([[makeQuery(id+"F5.imprint","IMPRINT",EDGE,{"disambiguationData":[TD([[subQ2,-1.0]])],"derivedFrom":subQ1}),1.0]])]});}
            var Q2;
            {var subQ0=sQuery(id+"F5.wireOp",EDGE,"E32");var subQ1=sQuery(id+"F5.wireOp",EDGE,"E13");var subQ2=makeQuery(id+"F5.imprint","INTERSECT",VERTEX,{"disambiguationData":[OD(0.0)],"derivedFrom":[subQ1,subQ0]});Q2=makeQuery(id+"F5.imprint","IMPRINT",FACE,{"disambiguationData":[TD([[makeQuery(id+"F5.imprint","IMPRINT",EDGE,{"disambiguationData":[TD([[subQ2,-1.0]])],"derivedFrom":subQ1}),-1.0]])]});}
            var Q3;
            {var subQ0=sQuery(id+"F5.wireOp",EDGE,"E32");var subQ1=sQuery(id+"F5.wireOp",EDGE,"E13");var subQ2=makeQuery(id+"F5.imprint","INTERSECT",VERTEX,{"disambiguationData":[OD(0.0)],"derivedFrom":[subQ1,subQ0]});Q3=makeQuery(id+"F5.imprint","IMPRINT",FACE,{"disambiguationData":[TD([[makeQuery(id+"F5.imprint","IMPRINT",EDGE,{"disambiguationData":[TD([[subQ2,-1.0]])],"derivedFrom":subQ1}),1.0]])]});}
            var Q4;
            {var subQ0=sQuery(id+"F5.wireOp",EDGE,"E33");var subQ1=sQuery(id+"F5.wireOp",EDGE,"E13");var subQ2=makeQuery(id+"F5.imprint","INTERSECT",VERTEX,{"disambiguationData":[OD(0.0)],"derivedFrom":[subQ1,subQ0]});Q4=makeQuery(id+"F5.imprint","IMPRINT",FACE,{"disambiguationData":[TD([[makeQuery(id+"F5.imprint","IMPRINT",EDGE,{"disambiguationData":[TD([[subQ2,-1.0]])],"derivedFrom":subQ1}),1.0]])]});}
            var Q5;
            {var subQ0=sQuery(id+"F5.wireOp",EDGE,"E33");var subQ1=sQuery(id+"F5.wireOp",EDGE,"E13");var subQ2=makeQuery(id+"F5.imprint","INTERSECT",VERTEX,{"disambiguationData":[OD(0.0)],"derivedFrom":[subQ1,subQ0]});Q5=makeQuery(id+"F5.imprint","IMPRINT",FACE,{"disambiguationData":[TD([[makeQuery(id+"F5.imprint","IMPRINT",EDGE,{"disambiguationData":[TD([[subQ2,-1.0]])],"derivedFrom":subQ1}),-1.0]])]});}
            var Q6;
            {var subQ0=sQuery(id+"F5.wireOp",EDGE,"E34");var subQ1=sQuery(id+"F5.wireOp",EDGE,"E13");var subQ2=makeQuery(id+"F5.imprint","INTERSECT",VERTEX,{"disambiguationData":[OD(0.0)],"derivedFrom":[subQ1,subQ0]});Q6=makeQuery(id+"F5.imprint","IMPRINT",FACE,{"disambiguationData":[TD([[makeQuery(id+"F5.imprint","IMPRINT",EDGE,{"disambiguationData":[TD([[subQ2,-1.0]])],"derivedFrom":subQ1}),1.0]])]});}
            var Q7;
            {var subQ0=sQuery(id+"F5.wireOp",EDGE,"E34");var subQ1=sQuery(id+"F5.wireOp",EDGE,"E13");var subQ2=makeQuery(id+"F5.imprint","INTERSECT",VERTEX,{"disambiguationData":[OD(0.0)],"derivedFrom":[subQ1,subQ0]});Q7=makeQuery(id+"F5.imprint","IMPRINT",FACE,{"disambiguationData":[TD([[makeQuery(id+"F5.imprint","IMPRINT",EDGE,{"disambiguationData":[TD([[subQ2,-1.0]])],"derivedFrom":subQ1}),-1.0]])]});}
            var Q8;
            {var subQ1=sQuery(id+"F5.wireOp",EDGE,"E36.bottom");Q8=makeQuery(id+"F5.imprint","IMPRINT",FACE,{"disambiguationData":[TD([[makeQuery(id+"F5.imprint","IMPRINT",EDGE,{"derivedFrom":subQ1}),-1.0]])]});}
            var Q9;
            {var subQ0=sQuery(id+"F5.wireOp",EDGE,"E36.top");var subQ1=sQuery(id+"F5.wireOp",EDGE,"E13");var subQ2=makeQuery(id+"F5.imprint","INTERSECT",VERTEX,{"derivedFrom":[subQ1,subQ0]});Q9=makeQuery(id+"F5.imprint","IMPRINT",FACE,{"disambiguationData":[TD([[makeQuery(id+"F5.imprint","IMPRINT",EDGE,{"disambiguationData":[TD([[subQ2,-1.0]])],"derivedFrom":subQ1}),1.0]])]});}
            var Q10;
            {var subQ0=sQuery(id+"F5.wireOp",EDGE,"E35");var subQ1=sQuery(id+"F5.wireOp",EDGE,"E13");var subQ2=makeQuery(id+"F5.imprint","INTERSECT",VERTEX,{"disambiguationData":[OD(0.0)],"derivedFrom":[subQ1,subQ0]});Q10=makeQuery(id+"F5.imprint","IMPRINT",FACE,{"disambiguationData":[TD([[makeQuery(id+"F5.imprint","IMPRINT",EDGE,{"disambiguationData":[TD([[subQ2,-1.0]])],"derivedFrom":subQ1}),-1.0]])]});}
            var Q11;
            {var subQ0=sQuery(id+"F5.wireOp",EDGE,"E35");var subQ1=sQuery(id+"F5.wireOp",EDGE,"E13");var subQ2=makeQuery(id+"F5.imprint","INTERSECT",VERTEX,{"disambiguationData":[OD(0.0)],"derivedFrom":[subQ1,subQ0]});Q11=makeQuery(id+"F5.imprint","IMPRINT",FACE,{"disambiguationData":[TD([[makeQuery(id+"F5.imprint","IMPRINT",EDGE,{"disambiguationData":[TD([[subQ2,-1.0]])],"derivedFrom":subQ1}),1.0]])]});}
            extrude(context, id + "F8", {"entities" : qUnion([Q0, Q1, Q2, Q3, Q4, Q5, Q6, Q7, Q8, Q9, Q10, Q11]), "operationType" : NewBodyOperationType.ADD, "depth" : 8 * mm, "offsetDistance" : 25 * mm});
        }
        {
            var Q0;
            Q0=makeQuery(id+"F8.opExtrude","CAP_EDGE",EDGE,{"disambiguationData":[OSD([sQuery(id+"F5.wireOp",EDGE,"E35")])],"isStart":false});
            var Q1;
            Q1=makeQuery(id+"F8.opExtrude","CAP_FACE",FACE,{"disambiguationData":[OSD([sQuery(id+"F5.wireOp",EDGE,"E31")])],"isStart":false});
            var Q2;
            Q2=makeQuery(id+"F8.opExtrude","CAP_FACE",FACE,{"disambiguationData":[OSD([sQuery(id+"F5.wireOp",EDGE,"E32")])],"isStart":false});
            var Q3;
            Q3=makeQuery(id+"F8.opExtrude","CAP_FACE",FACE,{"disambiguationData":[OSD([sQuery(id+"F5.wireOp",EDGE,"E33")])],"isStart":false});
            var Q4;
            Q4=makeQuery(id+"F8.opExtrude","CAP_FACE",FACE,{"disambiguationData":[OSD([sQuery(id+"F5.wireOp",EDGE,"E34")])],"isStart":false});
            var Q5;
            Q5=makeQuery(id+"F8.opExtrude","CAP_EDGE",EDGE,{"disambiguationData":[OSD([sQuery(id+"F5.wireOp",EDGE,"E36.left")])],"isStart":false});
            var Q6;
            Q6=makeQuery(id+"F8.opExtrude","CAP_EDGE",EDGE,{"disambiguationData":[OSD([sQuery(id+"F5.wireOp",EDGE,"E36.right")])],"isStart":false});
            var Q7;
            Q7=makeQuery(id+"F8.opExtrude","CAP_EDGE",EDGE,{"disambiguationData":[OSD([sQuery(id+"F5.wireOp",EDGE,"E36.bottom")])],"isStart":false});
            var Q8;
            Q8=makeQuery(id+"F8.opExtrude","CAP_EDGE",EDGE,{"disambiguationData":[OSD([sQuery(id+"F5.wireOp",EDGE,"E36.top")])],"isStart":false});
            fillet(context, id + "F9", {"entities" : qUnion([Q0, Q1, Q2, Q3, Q4, Q5, Q6, Q7, Q8]), "radius" : .45 * mm, "tangentPropagation" : true, "allowEdgeOverflow" : false});
        }
        {
            var Q0;
            Q0=qCreatedBy(makeId("Top.planeOp"),FACE);
            var sketch = newSketch(context, id + "F10", { "sketchPlane" : qUnion([Q0])});
            skCircle(sketch, "E37", {"center": v(0, 0) * mm, "radius": 4 * mm});
            skLineSegment(sketch, "E38", {"start": v(0, 0) * mm, "end": v(4.14, -15.45) * mm});
            skLineSegment(sketch, "E39.0", {"start": v(-2.13, -0.57) * mm, "end": v(2.25, -16.91) * mm});
            skLineSegment(sketch, "E40.0", {"start": v(2.13, 0.57) * mm, "end": v(6.4, -15.42) * mm});
            skCircle(sketch, "E41", {"center": v(2.6, -9.71) * mm, "radius": 5.95 * mm});
            skSolve(sketch);
        }
        {
            var Q0;
            {var subQ0=sQuery(id+"F10.wireOp",EDGE,"E37");var subQ1=makeQuery(id+"F10.imprint","INTERSECT",VERTEX,{"derivedFrom":[subQ0,sQuery(id+"F10.wireOp",EDGE,"E39.0")]});Q0=makeQuery(id+"F10.imprint","IMPRINT",FACE,{"disambiguationData":[TD([[makeQuery(id+"F10.imprint","IMPRINT",EDGE,{"disambiguationData":[TD([[subQ1,-1.0]])],"derivedFrom":subQ0}),1.0]])]});}
            var Q1;
            {var subQ0=sQuery(id+"F10.wireOp",EDGE,"E39.0");var subQ1=sQuery(id+"F10.wireOp",EDGE,"E37");var subQ2=makeQuery(id+"F10.imprint","INTERSECT",VERTEX,{"derivedFrom":[subQ1,subQ0]});Q1=makeQuery(id+"F10.imprint","IMPRINT",FACE,{"disambiguationData":[TD([[makeQuery(id+"F10.imprint","IMPRINT",EDGE,{"disambiguationData":[TD([[subQ2,-1.0]])],"derivedFrom":subQ1}),-1.0]])]});}
            var Q2;
            {var subQ0=sQuery(id+"F10.wireOp",EDGE,"E40.0");var subQ1=sQuery(id+"F10.wireOp",EDGE,"E37");var subQ2=makeQuery(id+"F10.imprint","INTERSECT",VERTEX,{"derivedFrom":[subQ1,subQ0]});Q2=makeQuery(id+"F10.imprint","IMPRINT",FACE,{"disambiguationData":[TD([[makeQuery(id+"F10.imprint","IMPRINT",EDGE,{"disambiguationData":[TD([[subQ2,1.0]])],"derivedFrom":subQ1}),-1.0]])]});}
            var Q3;
            {var subQ0=sQuery(id+"F10.wireOp",EDGE,"E41");var subQ1=sQuery(id+"F10.wireOp",EDGE,"E38");var subQ2=makeQuery(id+"F10.imprint","INTERSECT",VERTEX,{"disambiguationData":[OD(0.0)],"derivedFrom":[subQ1,subQ0]});Q3=makeQuery(id+"F10.imprint","IMPRINT",FACE,{"disambiguationData":[TD([[makeQuery(id+"F10.imprint","IMPRINT",EDGE,{"disambiguationData":[TD([[subQ2,1.0]])],"derivedFrom":subQ1}),1.0]])]});}
            var Q4;
            {var subQ0=sQuery(id+"F10.wireOp",EDGE,"E41");var subQ1=sQuery(id+"F10.wireOp",EDGE,"E38");var subQ2=makeQuery(id+"F10.imprint","INTERSECT",VERTEX,{"disambiguationData":[OD(0.0)],"derivedFrom":[subQ1,subQ0]});Q4=makeQuery(id+"F10.imprint","IMPRINT",FACE,{"disambiguationData":[TD([[makeQuery(id+"F10.imprint","IMPRINT",EDGE,{"disambiguationData":[TD([[subQ2,1.0]])],"derivedFrom":subQ1}),-1.0]])]});}
            extrude(context, id + "F11", {"entities" : qUnion([Q0, Q1, Q2, Q3, Q4]), "operationType" : NewBodyOperationType.REMOVE, "depth" : 1 * mm, "offsetDistance" : 25 * mm});
        }
        {
            var Q0;
            {var subQ0=sQuery(id+"F1.wireOp",EDGE,"E11");var subQ1=sQuery(id+"F1.wireOp",EDGE,"E12");var subQ2=sQuery(id+"F0.wireOp",EDGE,"E10");var subQ3=sQuery(id+"F0.wireOp",EDGE,"E1.0");var subQ4=sQuery(id+"F5.wireOp",EDGE,"E27");var subQ5=sQuery(id+"F5.wireOp",EDGE,"E28");Q0=makeQuery(id+"F6.boolean.opBoolean","SPLIT",EDGE,{"disambiguationData":[TD([makeQuery(id+"F2.opExtrude","SWEPT_FACE",FACE,{"disambiguationData":[OSD([subQ0])]}),makeQuery(id+"F2.opExtrude","CAP_FACE",FACE,{"disambiguationData":[OSD([subQ0,subQ1])],"isStart":true}),makeQuery(id+"F3.opExtrude","CAP_FACE",FACE,{"disambiguationData":[OSD([subQ3,sQuery(id+"F0.wireOp",EDGE,"E2.left"),sQuery(id+"F0.wireOp",EDGE,"E2.right"),subQ2])],"isStart":true}),makeQuery(id+"F3.opExtrude","CAP_FACE",FACE,{"disambiguationData":[OSD([subQ3,sQuery(id+"F0.wireOp",EDGE,"E7.bottom"),sQuery(id+"F0.wireOp",EDGE,"E7.top"),subQ2])],"isStart":true}),makeQuery(id+"F3.opExtrude","CAP_FACE",FACE,{"disambiguationData":[OSD([subQ3,sQuery(id+"F0.wireOp",EDGE,"E3.left"),sQuery(id+"F0.wireOp",EDGE,"E3.right"),subQ2])],"isStart":true}),makeQuery(id+"F3.opExtrude","CAP_FACE",FACE,{"disambiguationData":[OSD([subQ3,sQuery(id+"F0.wireOp",EDGE,"E8.left"),sQuery(id+"F0.wireOp",EDGE,"E8.right"),subQ2])],"isStart":true}),makeQuery(id+"F3.opExtrude","CAP_FACE",FACE,{"disambiguationData":[OSD([subQ3,sQuery(id+"F0.wireOp",EDGE,"E6.bottom"),sQuery(id+"F0.wireOp",EDGE,"E6.top"),subQ2])],"isStart":true}),makeQuery(id+"F3.opExtrude","CAP_FACE",FACE,{"disambiguationData":[OSD([subQ0,subQ1])],"isStart":true}),makeQuery(id+"F4.opExtrude","CAP_FACE",FACE,{"disambiguationData":[OSD([subQ0])],"isStart":true}),makeQuery(id+"F6.opExtrude","CAP_FACE",FACE,{"disambiguationData":[OSD([sQuery(id+"F5.wireOp",EDGE,"E25")])],"isStart":true}),makeQuery(id+"F6.opExtrude","CAP_FACE",FACE,{"disambiguationData":[OSD([sQuery(id+"F5.wireOp",EDGE,"E26")])],"isStart":true}),makeQuery(id+"F6.opExtrude","SWEPT_FACE",FACE,{"disambiguationData":[OSD([subQ4])]}),makeQuery(id+"F6.opExtrude","CAP_FACE",FACE,{"disambiguationData":[OSD([subQ4])],"isStart":true}),makeQuery(id+"F6.opExtrude","SWEPT_FACE",FACE,{"disambiguationData":[OSD([subQ5])]}),makeQuery(id+"F6.opExtrude","CAP_FACE",FACE,{"disambiguationData":[OSD([subQ5])],"isStart":true}),makeQuery(id+"F6.opExtrude","CAP_FACE",FACE,{"disambiguationData":[OSD([sQuery(id+"F5.wireOp",EDGE,"E29")])],"isStart":true}),makeQuery(id+"F6.opExtrude","CAP_FACE",FACE,{"disambiguationData":[OSD([sQuery(id+"F5.wireOp",EDGE,"E30")])],"isStart":true})])],"derivedFrom":makeQuery(id+"F2.opExtrude","CAP_EDGE",EDGE,{"disambiguationData":[OSD([subQ0])],"isStart":true})});}
            var Q1;
            Q1=makeQuery(id+"F11.boolean.opBoolean","COPY",EDGE,{"derivedFrom":makeQuery(id+"F11.opExtrude","CAP_EDGE",EDGE,{"disambiguationData":[OSD([sQuery(id+"F10.wireOp",EDGE,"E40.0")])],"isStart":true})});
            var Q2;
            Q2=makeQuery(id+"F11.boolean.opBoolean","COPY",EDGE,{"derivedFrom":makeQuery(id+"F11.opExtrude","CAP_EDGE",EDGE,{"disambiguationData":[OSD([sQuery(id+"F10.wireOp",EDGE,"E40.0")])],"isStart":false})});
            var Q3;
            Q3=makeQuery(id+"F11.boolean.opBoolean","COPY",EDGE,{"derivedFrom":makeQuery(id+"F11.opExtrude","CAP_EDGE",EDGE,{"disambiguationData":[OSD([sQuery(id+"F10.wireOp",EDGE,"E37")])],"isStart":true})});
            var Q4;
            Q4=makeQuery(id+"F11.boolean.opBoolean","COPY",EDGE,{"derivedFrom":makeQuery(id+"F11.opExtrude","CAP_EDGE",EDGE,{"disambiguationData":[OSD([sQuery(id+"F10.wireOp",EDGE,"E37")])],"isStart":false})});
            var Q5;
            Q5=makeQuery(id+"F11.boolean.opBoolean","COPY",EDGE,{"derivedFrom":makeQuery(id+"F11.opExtrude","CAP_EDGE",EDGE,{"disambiguationData":[OSD([sQuery(id+"F10.wireOp",EDGE,"E39.0")])],"isStart":true})});
            var Q6;
            Q6=makeQuery(id+"F11.boolean.opBoolean","COPY",EDGE,{"derivedFrom":makeQuery(id+"F11.opExtrude","CAP_EDGE",EDGE,{"disambiguationData":[OSD([sQuery(id+"F10.wireOp",EDGE,"E41")])],"isStart":false})});
            var Q7;
            Q7=makeQuery(id+"F11.boolean.opBoolean","COPY",EDGE,{"derivedFrom":makeQuery(id+"F11.opExtrude","CAP_EDGE",EDGE,{"disambiguationData":[OSD([sQuery(id+"F10.wireOp",EDGE,"E41")])],"isStart":true})});
            var Q8;
            Q8=makeQuery(id+"F11.boolean.opBoolean","COPY",EDGE,{"derivedFrom":makeQuery(id+"F11.opExtrude","CAP_EDGE",EDGE,{"disambiguationData":[OSD([sQuery(id+"F10.wireOp",EDGE,"E39.0")])],"isStart":false})});
            fillet(context, id + "F12", {"entities" : qUnion([Q0, Q1, Q2, Q3, Q4, Q5, Q6, Q7, Q8]), "radius" : .5 * mm, "tangentPropagation" : true, "allowEdgeOverflow" : false});
        }
    });
